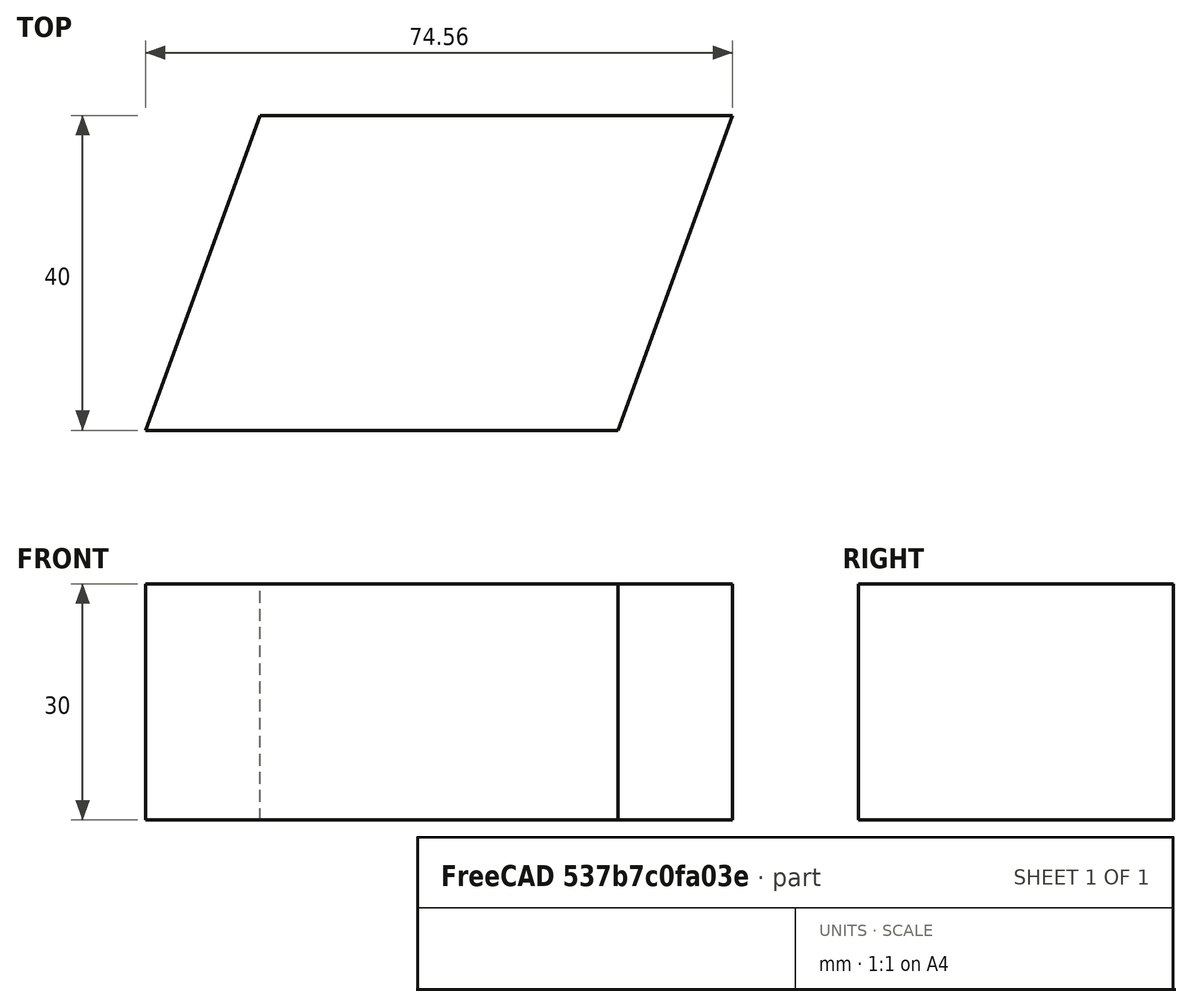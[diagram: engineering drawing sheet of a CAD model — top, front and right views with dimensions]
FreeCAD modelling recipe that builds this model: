
FCSTD DOCUMENT  (FreeCAD 0.19R)
Label: Rhomboid
License: All rights reserved
LicenseURL: http://en.wikipedia.org/wiki/All_rights_reserved
objects: Sketcher::SketchObject×1, PartDesign::Pad×1, PartDesign::Body×1
note: 4 computed .brp shape members not serialized (recipe doc carries the construction recipe); baked Part::Feature solids carry a one-line shape summary decoded from their .brp

FEATURE [Sketcher::SketchObject] Sketch
  FullyConstrained = true
  MapMode = 5
  Support = -> [XY_Plane]
  sketch-geometry (4):
    g0: LineSegment StartX=22.5588 StartY=48 StartZ=0 EndX=82.5588 EndY=48 EndZ=0
    g1: LineSegment StartX=82.5588 StartY=48 StartZ=0 EndX=68 EndY=8 EndZ=0
    g2: LineSegment StartX=68 StartY=8 StartZ=0 EndX=8 EndY=8 EndZ=0
    g3: LineSegment StartX=8 StartY=8 StartZ=0 EndX=22.5588 EndY=48 EndZ=0
  constraints (12):
    c: Coincident(g0,g1)
    c: Coincident(g1,g2)
    c: Coincident(g2,g3)
    c: Coincident(g3,g0)
    c: Horizontal(g0)
    c: Horizontal(g2)
    c: DistanceX(g-1,g2) = 8
    c: DistanceY(g-1,g2) = 8
    c: DistanceY(g1,g0) = 40
    c: DistanceX(g2,g1) = 60
    c: Equal(g1,g3)
    c: Angle(g2,g3) = 1.22173
FEATURE [PartDesign::Pad] Pad
  Direction = (1,1,1)
  Length = 30
  Length2 = 100
  Profile = -> Sketch
  Type = 0
FEATURE [PartDesign::Body] Body
  Group = -> [Sketch,Pad]
  Origin = -> Origin
  Tip = -> Pad
